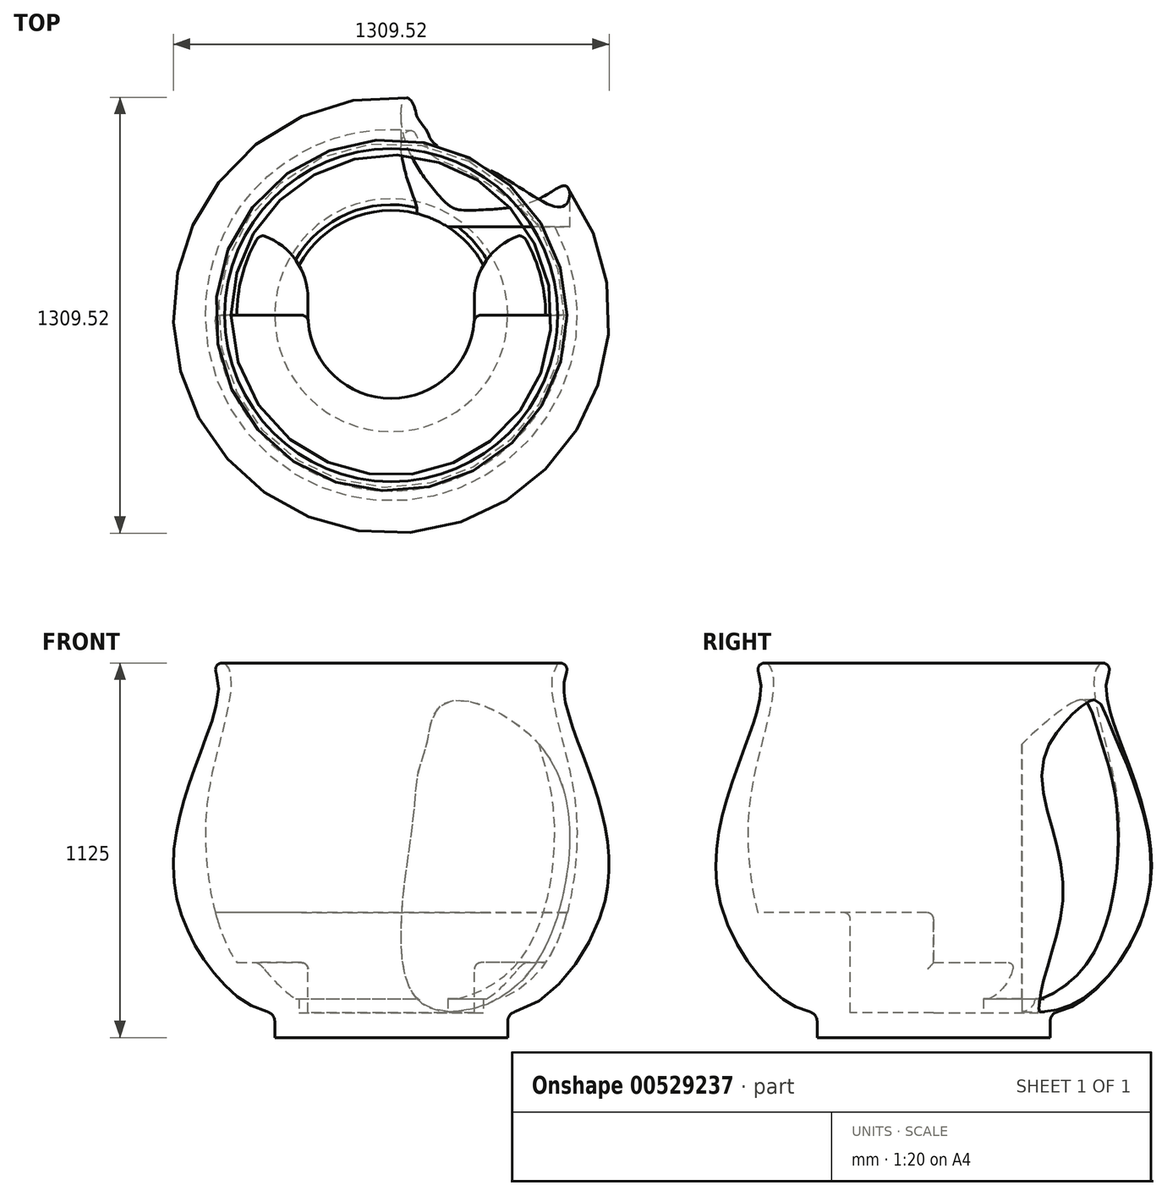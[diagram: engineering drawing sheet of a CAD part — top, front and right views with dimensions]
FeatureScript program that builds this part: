
annotation { "Feature Type Name" : "Feature", "Feature Type Description" : "" }
export const myFeature = defineFeature(function(context is Context, id is Id, definition is map)
    precondition{}
    {
        {
            var Q0;
            Q0=qCreatedBy(makeId("Front.planeOp"),FACE);
            var sketch = newSketch(context, id + "F0", { "sketchPlane" : qUnion([Q0])});
            skLineSegment(sketch, "E0", {"start": v(0, 0) * mm, "end": v(-350, 0) * mm});
            skLineSegment(sketch, "E1", {"start": v(-350, 0) * mm, "end": v(-350, 75) * mm});
            skFitSpline(sketch, "E2", {"points": [v(-350, 75) * mm, v(-650, 450) * mm, v(-525, 1000) * mm, v(-550, 1125) * mm], "startDerivative": vector(-857.65, 0) * mm, "endDerivative": vector(-472.5, 299.4) * mm});
            skLineSegment(sketch, "E3", {"start": v(-550, 1125) * mm, "end": v(0, 1125) * mm});
            skLineSegment(sketch, "E4", {"start": v(0, 1125) * mm, "end": v(0, 0) * mm});
            skSolve(sketch);
        }
        {
            var Q0;
            Q0=makeQuery(id+"F0.imprint","IMPRINT",FACE,{"disambiguationData":[TD([[makeQuery(id+"F0.imprint","IMPRINT",EDGE,{"derivedFrom":sQuery(id+"F0.wireOp",EDGE,"E0")}),-1.0]])]});
            var Q1;
            Q1=sQuery(id+"F0.wireOp",EDGE,"E3");
            var Q2;
            Q2=sQuery(id+"F0.wireOp",EDGE,"E0");
            var Q3;
            Q3=sQuery(id+"F0.wireOp",EDGE,"E2");
            var Q4;
            Q4=sQuery(id+"F0.wireOp",EDGE,"E1");
            var Q5;
            Q5=sQuery(id+"F0.wireOp",EDGE,"E4");
            revolve(context, id + "F1", {"entities" : qUnion([Q0]), "surfaceEntities" : qUnion([Q1, Q2, Q3, Q4]), "axis" : qUnion([Q5]), "revolveType" : RevolveType.FULL});
        }
        {
            var Q0;
            Q0=makeQuery(id+"F1.opRevolve","SWEPT_EDGE",EDGE,{"disambiguationData":[OSD([sQuery(id+"F0.wireOp",VERTEX,"E2.end")])]});
            var Q1;
            Q1=makeQuery(id+"F1.opRevolve","SWEPT_EDGE",EDGE,{"disambiguationData":[OSD([sQuery(id+"F0.wireOp",EDGE,"E2"),sQuery(id+"F0.wireOp",EDGE,"E3")])]});
            fillet(context, id + "F2", {"entities" : qUnion([Q0, Q1]), "radius" : 20 * mm, "tangentPropagation" : true, "allowEdgeOverflow" : false});
        }
        {
            var Q0;
            Q0=makeQuery(id+"F1.opRevolve","SWEPT_EDGE",EDGE,{"disambiguationData":[OSD([sQuery(id+"F0.wireOp",VERTEX,"E1.end")])]});
            var Q1;
            Q1=makeQuery(id+"F1.opRevolve","SWEPT_EDGE",EDGE,{"disambiguationData":[OSD([sQuery(id+"F0.wireOp",EDGE,"E1"),sQuery(id+"F0.wireOp",EDGE,"E2")])]});
            fillet(context, id + "F3", {"entities" : qUnion([Q0, Q1]), "radius" : 30 * mm, "tangentPropagation" : true, "allowEdgeOverflow" : false});
        }
        {
            var Q0;
            Q0=qCreatedBy(makeId("Front.planeOp"),FACE);
            var sketch = newSketch(context, id + "F4", { "sketchPlane" : qUnion([Q0])});
            skFitSpline(sketch, "E5", {"points": [v(-500, 1125) * mm, v(-512.75, 897.4) * mm, v(-558.18, 615.07) * mm, v(-460.82, 220.77) * mm, v(-332.1, 116.93) * mm], "startDerivative": vector(492.93, -428.25) * mm, "endDerivative": vector(298.16, -78.24) * mm});
            skLineSegment(sketch, "E6", {"start": v(-500, 1125) * mm, "end": v(0, 1125) * mm});
            skLineSegment(sketch, "E7", {"start": v(0, 1125) * mm, "end": v(0, 75) * mm});
            skLineSegment(sketch, "E8", {"start": v(0, 75) * mm, "end": v(-315, 75) * mm});
            skLineSegment(sketch, "E9", {"start": v(-315, 75) * mm, "end": v(-315, 116.93) * mm});
            skLineSegment(sketch, "E10", {"start": v(-315, 116.93) * mm, "end": v(-332.1, 116.93) * mm});
            skSolve(sketch);
        }
        {
            var Q0;
            Q0 = qSketchRegion(id + "F4", true);
            var Q1;
            Q1=sQuery(id+"F4.wireOp",EDGE,"E7");
            revolve(context, id + "F5", {"operationType" : NewBodyOperationType.REMOVE, "entities" : qUnion([Q0]), "axis" : qUnion([Q1]), "revolveType" : RevolveType.FULL, "oppositeDirection" : true});
        }
        {
            var Q0;
            Q0=makeQuery(id+"F5.boolean.opBoolean","COPY",FACE,{"derivedFrom":makeQuery(id+"F5.opRevolve","SWEPT_FACE",FACE,{"disambiguationData":[OSD([sQuery(id+"F4.wireOp",EDGE,"E8")])]})});
            cPlane(context, id + "F6", {"entities" : qUnion([Q0]), "cplaneType" : CPlaneType.OFFSET, "offset" : 300 * mm, "width" : 150 * mm, "height" : 150 * mm});
        }
        {
            var Q0;
            Q0=qCreatedBy(id+"F6.planeOp",FACE);
            var sketch = newSketch(context, id + "F7", { "sketchPlane" : qUnion([Q0])});
            skArc(sketch, "E11", {"start": v(-550, 0) * mm, "mid": v(0, -550) * mm, "end": v(550, 0) * mm});
            skArc(sketch, "E12", {"start": v(-250, 0) * mm, "mid": v(0, -250) * mm, "end": v(250, 0) * mm});
            skLineSegment(sketch, "E13", {"start": v(-250, 0) * mm, "end": v(-550, 0) * mm});
            skLineSegment(sketch, "E14", {"start": v(250, 0) * mm, "end": v(550, 0) * mm});
            skSolve(sketch);
        }
        {
            var Q0;
            Q0 = qSketchRegion(id + "F7", true);
            extrude(context, id + "F8", {"entities" : qUnion([Q0]), "operationType" : NewBodyOperationType.ADD, "endBound" : BoundingType.UP_TO_NEXT, "oppositeDirection" : true, "depth" : 25 * mm, "offsetDistance" : 25 * mm});
        }
        {
            var Q0;
            Q0=qCreatedBy(id+"F6.planeOp",FACE);
            cPlane(context, id + "F9", {"entities" : qUnion([Q0]), "cplaneType" : CPlaneType.OFFSET, "offset" : 150 * mm, "oppositeDirection" : true, "width" : 150 * mm, "height" : 150 * mm});
        }
        {
            var Q0;
            Q0=qCreatedBy(id+"F9.planeOp",FACE);
            var sketch = newSketch(context, id + "F10", { "sketchPlane" : qUnion([Q0])});
            skLineSegment(sketch, "E15", {"start": v(-250, 0) * mm, "end": v(-250, 50) * mm});
            skLineSegment(sketch, "E16", {"start": v(-450, 250) * mm, "end": v(-485.26, 250) * mm});
            skLineSegment(sketch, "E17", {"start": v(-528.44, 133.76) * mm, "end": v(-528.44, 0) * mm});
            skLineSegment(sketch, "E18", {"start": v(-528.44, 0) * mm, "end": v(-250, 0) * mm});
            skLineSegment(sketch, "E19", {"start": v(0, 0) * mm, "end": v(0, -250.3) * mm, "construction": true});
            skArc(sketch, "E20", {"start": v(-485.26, 250) * mm, "mid": v(-518.08, 191.38) * mm, "end": v(-528.44, 125) * mm});
            skPoint(sketch, "E21.orphan", {"position": v(-528.44, 250) * mm});
            skArc(sketch, "E22.MirrorCS", {"start": v(485.26, 250) * mm, "mid": v(518.08, 191.38) * mm, "end": v(528.44, 125) * mm});
            skPoint(sketch, "E23.MirrorP", {"position": v(528.44, 250) * mm});
            skLineSegment(sketch, "E24.MirrorCS", {"start": v(450, 250) * mm, "end": v(485.26, 250) * mm});
            skLineSegment(sketch, "E25.MirrorCS", {"start": v(528.44, 133.76) * mm, "end": v(528.44, 0) * mm});
            skLineSegment(sketch, "E26.MirrorCS", {"start": v(250, 0) * mm, "end": v(250, 50) * mm});
            skLineSegment(sketch, "E27.MirrorCS", {"start": v(528.44, 0) * mm, "end": v(250, 0) * mm});
            skPoint(sketch, "E28.visualSharp", {"position": v(-250, 250) * mm});
            skArc(sketch, "E28.filletArc", {"start": v(-250, 50) * mm, "mid": v(-308.58, 191.42) * mm, "end": v(-450, 250) * mm});
            skPoint(sketch, "E29.visualSharp", {"position": v(250, 250) * mm});
            skArc(sketch, "E29.filletArc", {"start": v(450, 250) * mm, "mid": v(308.58, 191.42) * mm, "end": v(250, 50) * mm});
            skSolve(sketch);
        }
        {
            var Q0;
            Q0 = qSketchRegion(id + "F10", true);
            extrude(context, id + "F11", {"entities" : qUnion([Q0]), "operationType" : NewBodyOperationType.ADD, "endBound" : BoundingType.UP_TO_NEXT, "oppositeDirection" : true, "depth" : 25 * mm, "offsetDistance" : 25 * mm});
        }
        {
            var Q0;
            Q0=makeQuery(id+"F8.opExtrude","CAP_EDGE",EDGE,{"disambiguationData":[OSD([sQuery(id+"F7.wireOp",EDGE,"E12")])],"isStart":true});
            var Q1;
            Q1=makeQuery(id+"F11.opExtrude","CAP_EDGE",EDGE,{"disambiguationData":[OSD([sQuery(id+"F10.wireOp",EDGE,"E15")])],"isStart":true});
            var Q2;
            Q2=makeQuery(id+"F11.opExtrude","CAP_EDGE",EDGE,{"disambiguationData":[OSD([sQuery(id+"F10.wireOp",EDGE,"E26.MirrorCS")])],"isStart":true});
            var Q3;
            Q3=makeQuery(id+"F11.opExtrude","CAP_EDGE",EDGE,{"disambiguationData":[OSD([sQuery(id+"F10.wireOp",EDGE,"E29.filletArc")])],"isStart":true});
            var Q4;
            Q4=makeQuery(id+"F11.opExtrude","CAP_EDGE",EDGE,{"disambiguationData":[OSD([sQuery(id+"F10.wireOp",EDGE,"E28.filletArc")])],"isStart":true});
            var Q5;
            Q5=makeQuery(id+"F8.opExtrude","CAP_EDGE",EDGE,{"disambiguationData":[OSD([sQuery(id+"F7.wireOp",EDGE,"E13")])],"isStart":true});
            var Q6;
            Q6=makeQuery(id+"F8.opExtrude","CAP_EDGE",EDGE,{"disambiguationData":[OSD([sQuery(id+"F7.wireOp",EDGE,"E14")])],"isStart":true});
            var Q7;
            Q7=makeQuery(id+"F11.boolean.opBoolean","SPLIT",EDGE,{"derivedFrom":makeQuery(id+"F8.opExtrude","SWEPT_EDGE",EDGE,{"disambiguationData":[OSD([sQuery(id+"F7.wireOp",EDGE,"E12"),sQuery(id+"F7.wireOp",EDGE,"E14")])]})});
            var Q8;
            Q8=makeQuery(id+"F11.boolean.opBoolean","SPLIT",EDGE,{"derivedFrom":makeQuery(id+"F8.opExtrude","SWEPT_EDGE",EDGE,{"disambiguationData":[OSD([sQuery(id+"F7.wireOp",EDGE,"E12"),sQuery(id+"F7.wireOp",EDGE,"E13")])]})});
            fillet(context, id + "F12", {"entities" : qUnion([Q0, Q1, Q2, Q3, Q4, Q5, Q6, Q7, Q8]), "radius" : 20 * mm, "tangentPropagation" : true, "allowEdgeOverflow" : false});
        }
        {
            var Q0;
            Q0=qCreatedBy(makeId("Front.planeOp"),FACE);
            var sketch = newSketch(context, id + "F13", { "sketchPlane" : qUnion([Q0])});
            skFitSpline(sketch, "E30", {"points": [v(95.55, 842.99) * mm, v(240.68, 888.78) * mm, v(391.14, 848.96) * mm, v(471.75, 448.86) * mm, v(301.56, 159.24) * mm, v(137.35, 177.16) * mm, v(70.17, 629.5) * mm, v(95.55, 842.99) * mm]});
            skSolve(sketch);
        }
        {
            var Q0;
            Q0=qCreatedBy(makeId("Front.planeOp"),FACE);
            cPlane(context, id + "F14", {"entities" : qUnion([Q0]), "cplaneType" : CPlaneType.OFFSET, "offset" : 265 * mm, "oppositeDirection" : true, "width" : 150 * mm, "height" : 150 * mm});
        }
        {
            var Q0;
            Q0=qCreatedBy(id+"F14.planeOp",FACE);
            var sketch = newSketch(context, id + "F15", { "sketchPlane" : qUnion([Q0])});
            skFitSpline(sketch, "E31.0", {"points": [v(95.55, 842.99) * mm, v(109.17, 890.38) * mm, v(158.14, 1005.52) * mm, v(454.32, 868.7) * mm, v(519.88, 447.02) * mm, v(337.7, 126.18) * mm, v(69.75, 126.1) * mm, v(64.78, 643.4) * mm, v(78.36, 783.18) * mm, v(95.55, 842.99) * mm]});
            skSolve(sketch);
        }
        {
            var Q0;
            Q0 = qSketchRegion(id + "F15", true);
            extrude(context, id + "F16", {"entities" : qUnion([Q0]), "operationType" : NewBodyOperationType.REMOVE, "endBound" : BoundingType.THROUGH_ALL, "oppositeDirection" : true, "depth" : 25 * mm, "offsetDistance" : 25 * mm});
        }
    });
